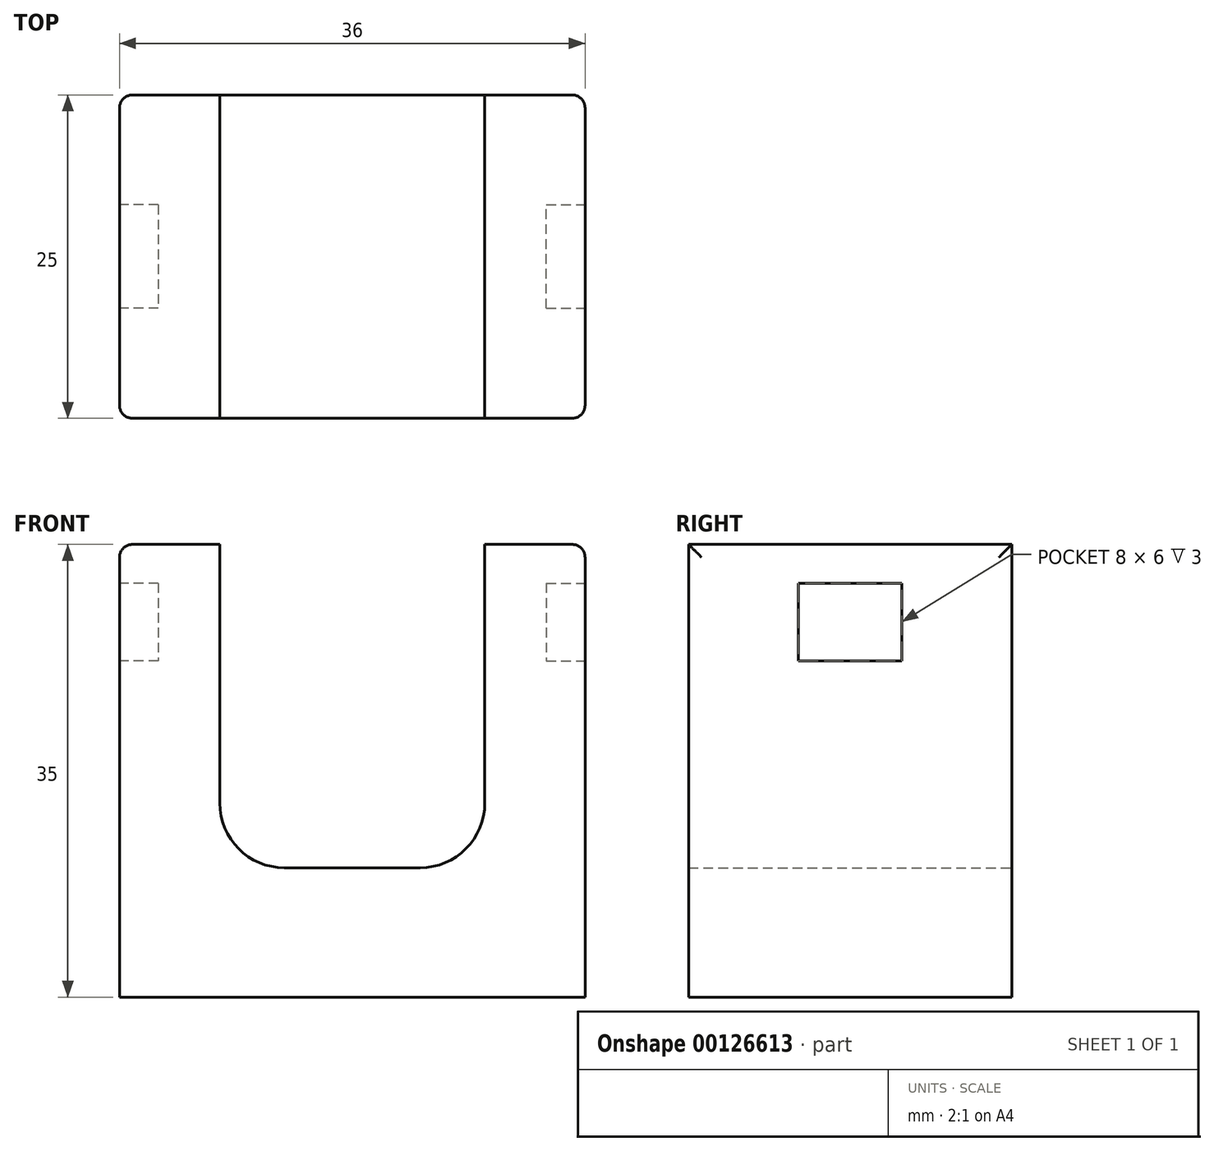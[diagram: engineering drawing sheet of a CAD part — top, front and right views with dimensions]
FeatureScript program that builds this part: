
annotation { "Feature Type Name" : "Feature", "Feature Type Description" : "" }
export const myFeature = defineFeature(function(context is Context, id is Id, definition is map)
    precondition{}
    {
        {
            var Q0;
            Q0=qCreatedBy(makeId("Top.planeOp"),FACE);
            var sketch = newSketch(context, id + "F0", { "sketchPlane" : qUnion([Q0])});
            skLineSegment(sketch, "E0.bottom", {"start": v(0, 0) * mm, "end": v(36, 0) * mm});
            skLineSegment(sketch, "E0.top", {"start": v(0, 25) * mm, "end": v(36, 25) * mm});
            skLineSegment(sketch, "E0.left", {"start": v(0, 0) * mm, "end": v(0, 25) * mm});
            skLineSegment(sketch, "E0.right", {"start": v(36, 0) * mm, "end": v(36, 25) * mm});
            skSolve(sketch);
        }
        {
            var Q0;
            Q0=makeQuery(id+"F0.imprint","IMPRINT",FACE,{"disambiguationData":[TD([[makeQuery(id+"F0.imprint","IMPRINT",EDGE,{"derivedFrom":sQuery(id+"F0.wireOp",EDGE,"E0.bottom")}),1.0]])]});
            extrude(context, id + "F1", {"entities" : qUnion([Q0]), "depth" : 35 * mm});
        }
        {
            var Q0;
            Q0=makeQuery(id+"F1.opExtrude","CAP_FACE",FACE,{"disambiguationData":[OSD([sQuery(id+"F0.wireOp",EDGE,"E0.bottom"),sQuery(id+"F0.wireOp",EDGE,"E0.top"),sQuery(id+"F0.wireOp",EDGE,"E0.left"),sQuery(id+"F0.wireOp",EDGE,"E0.right")])],"isStart":false});
            var sketch = newSketch(context, id + "F2", { "sketchPlane" : qUnion([Q0])});
            skLineSegment(sketch, "E1.bottom", {"start": v(7.75, 0) * mm, "end": v(28.25, 0) * mm});
            skLineSegment(sketch, "E1.top", {"start": v(7.75, 25) * mm, "end": v(28.25, 25) * mm});
            skLineSegment(sketch, "E1.left", {"start": v(7.75, 0) * mm, "end": v(7.75, 25) * mm});
            skLineSegment(sketch, "E1.right", {"start": v(28.25, 0) * mm, "end": v(28.25, 25) * mm});
            skLineSegment(sketch, "E2", {"start": v(7.75, 13.69) * mm, "end": v(0, 13.69) * mm, "construction": true});
            skLineSegment(sketch, "E3", {"start": v(28.25, 13.24) * mm, "end": v(36, 13.24) * mm, "construction": true});
            skSolve(sketch);
        }
        {
            var Q0;
            Q0 = qSketchRegion(id + "F2", true);
            extrude(context, id + "F3", {"entities" : qUnion([Q0]), "operationType" : NewBodyOperationType.REMOVE, "oppositeDirection" : true, "depth" : 25 * mm});
        }
        {
            var Q0;
            Q0=makeQuery(id+"F1.opExtrude","SWEPT_EDGE",EDGE,{"disambiguationData":[OSD([sQuery(id+"F0.wireOp",EDGE,"E0.bottom"),sQuery(id+"F0.wireOp",EDGE,"E0.left")])]});
            var Q1;
            Q1=makeQuery(id+"F1.opExtrude","CAP_EDGE",EDGE,{"disambiguationData":[OSD([sQuery(id+"F0.wireOp",EDGE,"E0.left")])],"isStart":false});
            var Q2;
            Q2=makeQuery(id+"F1.opExtrude","SWEPT_EDGE",EDGE,{"disambiguationData":[OSD([sQuery(id+"F0.wireOp",EDGE,"E0.top"),sQuery(id+"F0.wireOp",EDGE,"E0.left")])]});
            var Q3;
            Q3=makeQuery(id+"F1.opExtrude","SWEPT_EDGE",EDGE,{"disambiguationData":[OSD([sQuery(id+"F0.wireOp",EDGE,"E0.top"),sQuery(id+"F0.wireOp",EDGE,"E0.right")])]});
            var Q4;
            Q4=makeQuery(id+"F1.opExtrude","CAP_EDGE",EDGE,{"disambiguationData":[OSD([sQuery(id+"F0.wireOp",EDGE,"E0.right")])],"isStart":false});
            var Q5;
            Q5=makeQuery(id+"F1.opExtrude","SWEPT_EDGE",EDGE,{"disambiguationData":[OSD([sQuery(id+"F0.wireOp",EDGE,"E0.bottom"),sQuery(id+"F0.wireOp",EDGE,"E0.right")])]});
            fillet(context, id + "F4", {"entities" : qUnion([Q0, Q1, Q2, Q3, Q4, Q5]), "radius" : 1 * mm, "tangentPropagation" : true, "allowEdgeOverflow" : false});
        }
        {
            var Q0;
            Q0=makeQuery(id+"F3.boolean.opBoolean","COPY",EDGE,{"derivedFrom":makeQuery(id+"F3.opExtrude","CAP_EDGE",EDGE,{"disambiguationData":[OSD([sQuery(id+"F2.wireOp",EDGE,"E1.left")])],"isStart":false})});
            var Q1;
            Q1=makeQuery(id+"F3.boolean.opBoolean","COPY",EDGE,{"derivedFrom":makeQuery(id+"F3.opExtrude","CAP_EDGE",EDGE,{"disambiguationData":[OSD([sQuery(id+"F2.wireOp",EDGE,"E1.right")])],"isStart":false})});
            fillet(context, id + "F5", {"entities" : qUnion([Q0, Q1]), "radius" : 5 * mm, "tangentPropagation" : true, "allowEdgeOverflow" : false});
        }
        {
            var Q0;
            Q0=makeQuery(id+"F1.opExtrude","SWEPT_FACE",FACE,{"disambiguationData":[OSD([sQuery(id+"F0.wireOp",EDGE,"E0.left")])]});
            var sketch = newSketch(context, id + "F6", { "sketchPlane" : qUnion([Q0])});
            skLineSegment(sketch, "E4", {"start": v(-12.5, 32) * mm, "end": v(-16.5, 32) * mm, "construction": true});
            skLineSegment(sketch, "E5.bottom", {"start": v(-16.5, 32) * mm, "end": v(-8.5, 32) * mm, "construction": true});
            skLineSegment(sketch, "E5.top", {"start": v(-16.5, 26) * mm, "end": v(-8.5, 26) * mm, "construction": true});
            skLineSegment(sketch, "E5.left", {"start": v(-16.5, 32) * mm, "end": v(-16.5, 26) * mm, "construction": true});
            skLineSegment(sketch, "E5.right", {"start": v(-8.5, 32) * mm, "end": v(-8.5, 26) * mm, "construction": true});
            skLineSegment(sketch, "E6.bottom", {"start": v(-16.5, 32) * mm, "end": v(-8.5, 32) * mm});
            skLineSegment(sketch, "E6.top", {"start": v(-16.5, 26) * mm, "end": v(-8.5, 26) * mm});
            skLineSegment(sketch, "E6.left", {"start": v(-16.5, 32) * mm, "end": v(-16.5, 26) * mm});
            skLineSegment(sketch, "E6.right", {"start": v(-8.5, 32) * mm, "end": v(-8.5, 26) * mm});
            skLineSegment(sketch, "E7", {"start": v(-8.5, 32) * mm, "end": v(-1, 32) * mm, "construction": true});
            skLineSegment(sketch, "E8", {"start": v(-16.5, 32) * mm, "end": v(-24, 32) * mm, "construction": true});
            skSolve(sketch);
        }
        {
            var Q0;
            Q0=makeQuery(id+"F6.imprint","IMPRINT",FACE,{"disambiguationData":[TD([[makeQuery(id+"F6.imprint","IMPRINT",EDGE,{"derivedFrom":sQuery(id+"F6.wireOp",EDGE,"E6.bottom")}),-1.0]])]});
            extrude(context, id + "F7", {"entities" : qUnion([Q0]), "operationType" : NewBodyOperationType.REMOVE, "oppositeDirection" : true, "depth" : 3 * mm});
        }
        {
            var Q0;
            Q0=makeQuery(id+"F1.opExtrude","SWEPT_FACE",FACE,{"disambiguationData":[OSD([sQuery(id+"F0.wireOp",EDGE,"E0.right")])]});
            var sketch = newSketch(context, id + "F8", { "sketchPlane" : qUnion([Q0])});
            skLineSegment(sketch, "E9", {"start": v(12.5, 34) * mm, "end": v(12.5, 32) * mm, "construction": true});
            skLineSegment(sketch, "E10", {"start": v(12.5, 32) * mm, "end": v(8.5, 32) * mm, "construction": true});
            skLineSegment(sketch, "E11.bottom", {"start": v(8.5, 32) * mm, "end": v(16.5, 32) * mm, "construction": true});
            skLineSegment(sketch, "E11.top", {"start": v(8.5, 26) * mm, "end": v(16.5, 26) * mm, "construction": true});
            skLineSegment(sketch, "E11.left", {"start": v(8.5, 32) * mm, "end": v(8.5, 26) * mm, "construction": true});
            skLineSegment(sketch, "E11.right", {"start": v(16.5, 32) * mm, "end": v(16.5, 26) * mm, "construction": true});
            skLineSegment(sketch, "E12", {"start": v(8.5, 32) * mm, "end": v(1, 32) * mm, "construction": true});
            skLineSegment(sketch, "E13", {"start": v(16.5, 32) * mm, "end": v(24, 32) * mm, "construction": true});
            skLineSegment(sketch, "E14.bottom", {"start": v(8.5, 32) * mm, "end": v(16.5, 32) * mm});
            skLineSegment(sketch, "E14.top", {"start": v(8.5, 26) * mm, "end": v(16.5, 26) * mm});
            skLineSegment(sketch, "E14.left", {"start": v(8.5, 32) * mm, "end": v(8.5, 26) * mm});
            skLineSegment(sketch, "E14.right", {"start": v(16.5, 32) * mm, "end": v(16.5, 26) * mm});
            skSolve(sketch);
        }
        {
            var Q0;
            Q0 = qSketchRegion(id + "F8", true);
            extrude(context, id + "F9", {"entities" : qUnion([Q0]), "operationType" : NewBodyOperationType.REMOVE, "oppositeDirection" : true, "depth" : 3 * mm});
        }
    });
